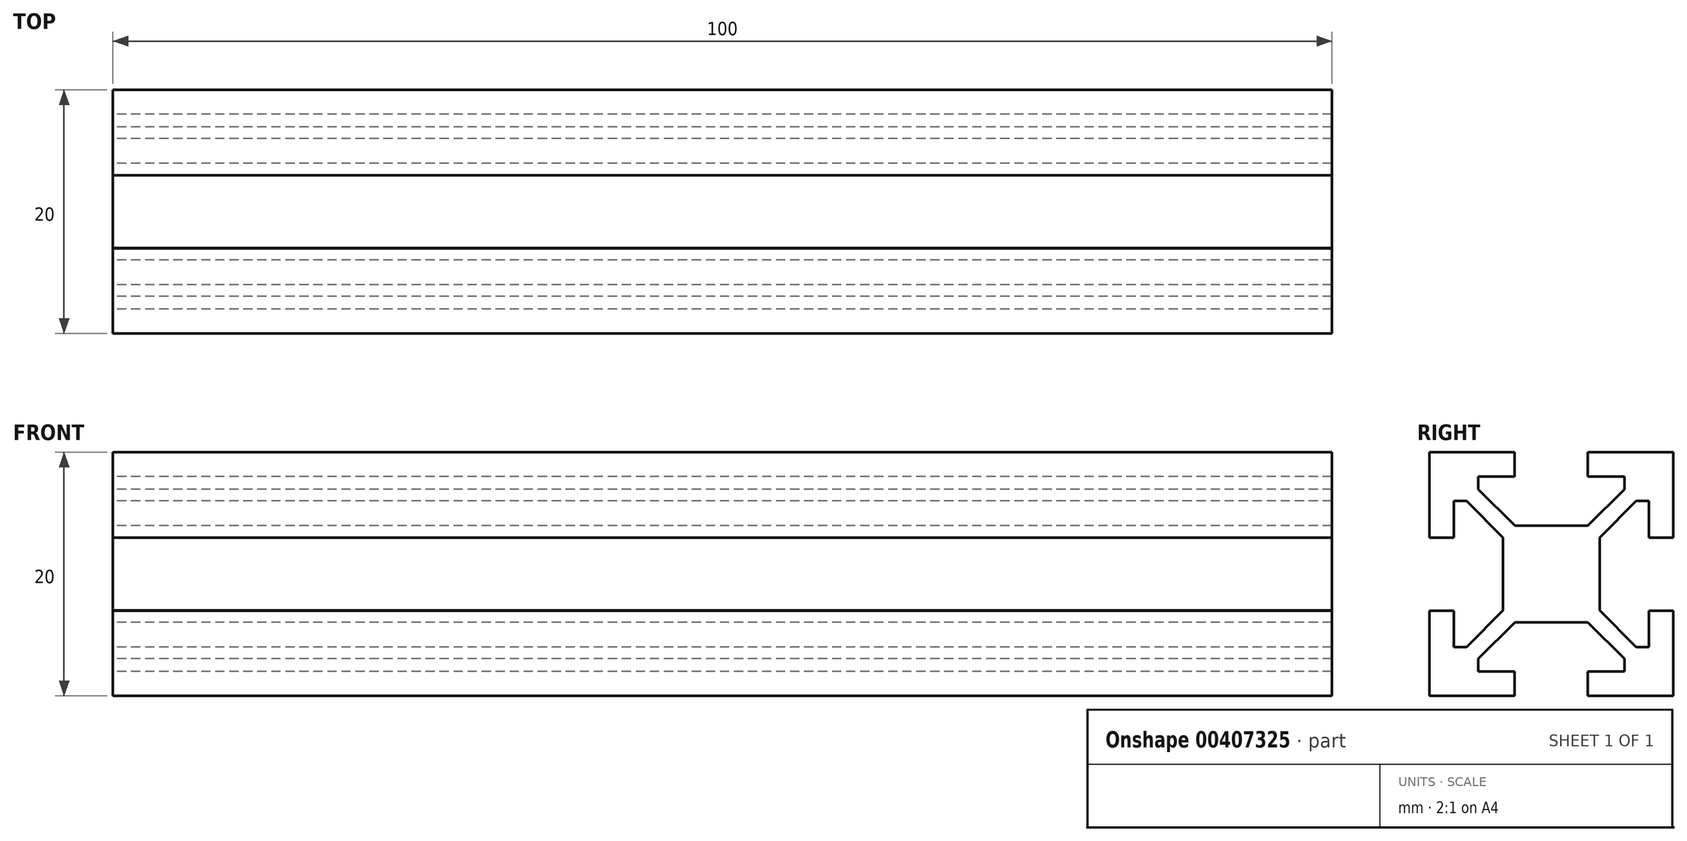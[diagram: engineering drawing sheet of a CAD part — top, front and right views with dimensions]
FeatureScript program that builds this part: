
annotation { "Feature Type Name" : "Feature", "Feature Type Description" : "" }
export const myFeature = defineFeature(function(context is Context, id is Id, definition is map)
    precondition{}
    {
        {
            var Q0;
            Q0=qCreatedBy(makeId("Right.planeOp"),FACE);
            var sketch = newSketch(context, id + "F0", { "sketchPlane" : qUnion([Q0])});
            skLineSegment(sketch, "E0", {"start": v(0, 3.96) * mm, "end": v(-3, 3.96) * mm});
            skLineSegment(sketch, "E1", {"start": v(-3, 3.96) * mm, "end": v(-6, 6.96) * mm});
            skLineSegment(sketch, "E2", {"start": v(-6, 6.96) * mm, "end": v(-6, 8) * mm});
            skLineSegment(sketch, "E3", {"start": v(-6, 8) * mm, "end": v(-3, 8) * mm});
            skLineSegment(sketch, "E4", {"start": v(-3, 8) * mm, "end": v(-3, 10) * mm});
            skLineSegment(sketch, "E5", {"start": v(-3, 10) * mm, "end": v(-10, 10) * mm});
            skLineSegment(sketch, "E6", {"start": v(0, 3.96) * mm, "end": v(0, 0) * mm, "construction": true});
            skLineSegment(sketch, "E7.MirrorCS", {"start": v(3, 8) * mm, "end": v(3, 10) * mm});
            skLineSegment(sketch, "E8.MirrorCS", {"start": v(6, 6.96) * mm, "end": v(6, 8) * mm});
            skLineSegment(sketch, "E9.MirrorCS", {"start": v(6, 8) * mm, "end": v(3, 8) * mm});
            skLineSegment(sketch, "E10.MirrorCS", {"start": v(0, 3.96) * mm, "end": v(3, 3.96) * mm});
            skLineSegment(sketch, "E11.MirrorCS", {"start": v(3, 10) * mm, "end": v(10, 10) * mm});
            skLineSegment(sketch, "E12.MirrorCS", {"start": v(3, 3.96) * mm, "end": v(6, 6.96) * mm});
            skLineSegment(sketch, "E13.1.0", {"start": v(-10, -3) * mm, "end": v(-10, -10) * mm});
            skLineSegment(sketch, "E13.1.1", {"start": v(-8, 3) * mm, "end": v(-10, 3) * mm});
            skLineSegment(sketch, "E13.1.2", {"start": v(-3.96, 0) * mm, "end": v(-3.96, -3) * mm});
            skLineSegment(sketch, "E13.1.3", {"start": v(-10, 3) * mm, "end": v(-10, 10) * mm});
            skLineSegment(sketch, "E13.1.4", {"start": v(-3.96, -3) * mm, "end": v(-6.96, -6) * mm});
            skLineSegment(sketch, "E13.1.5", {"start": v(-8, -6) * mm, "end": v(-8, -3) * mm});
            skLineSegment(sketch, "E13.1.6", {"start": v(-6.96, -6) * mm, "end": v(-8, -6) * mm});
            skLineSegment(sketch, "E13.1.7", {"start": v(-3.96, 3) * mm, "end": v(-6.96, 6) * mm});
            skLineSegment(sketch, "E13.1.8", {"start": v(-3.96, 0) * mm, "end": v(-3.96, 3) * mm});
            skLineSegment(sketch, "E13.1.9", {"start": v(-6.96, 6) * mm, "end": v(-8, 6) * mm});
            skLineSegment(sketch, "E13.1.10", {"start": v(-8, 6) * mm, "end": v(-8, 3) * mm});
            skLineSegment(sketch, "E13.1.11", {"start": v(-8, -3) * mm, "end": v(-10, -3) * mm});
            skLineSegment(sketch, "E13.2.0", {"start": v(3, -10) * mm, "end": v(10, -10) * mm});
            skLineSegment(sketch, "E13.2.1", {"start": v(-3, -8) * mm, "end": v(-3, -10) * mm});
            skLineSegment(sketch, "E13.2.2", {"start": v(0, -3.96) * mm, "end": v(3, -3.96) * mm});
            skLineSegment(sketch, "E13.2.3", {"start": v(-3, -10) * mm, "end": v(-10, -10) * mm});
            skLineSegment(sketch, "E13.2.4", {"start": v(3, -3.96) * mm, "end": v(6, -6.96) * mm});
            skLineSegment(sketch, "E13.2.5", {"start": v(6, -8) * mm, "end": v(3, -8) * mm});
            skLineSegment(sketch, "E13.2.6", {"start": v(6, -6.96) * mm, "end": v(6, -8) * mm});
            skLineSegment(sketch, "E13.2.7", {"start": v(-3, -3.96) * mm, "end": v(-6, -6.96) * mm});
            skLineSegment(sketch, "E13.2.8", {"start": v(0, -3.96) * mm, "end": v(-3, -3.96) * mm});
            skLineSegment(sketch, "E13.2.9", {"start": v(-6, -6.96) * mm, "end": v(-6, -8) * mm});
            skLineSegment(sketch, "E13.2.10", {"start": v(-6, -8) * mm, "end": v(-3, -8) * mm});
            skLineSegment(sketch, "E13.2.11", {"start": v(3, -8) * mm, "end": v(3, -10) * mm});
            skLineSegment(sketch, "E13.3.0", {"start": v(10, 3) * mm, "end": v(10, 10) * mm});
            skLineSegment(sketch, "E13.3.1", {"start": v(8, -3) * mm, "end": v(10, -3) * mm});
            skLineSegment(sketch, "E13.3.2", {"start": v(3.96, 0) * mm, "end": v(3.96, 3) * mm});
            skLineSegment(sketch, "E13.3.3", {"start": v(10, -3) * mm, "end": v(10, -10) * mm});
            skLineSegment(sketch, "E13.3.4", {"start": v(3.96, 3) * mm, "end": v(6.96, 6) * mm});
            skLineSegment(sketch, "E13.3.5", {"start": v(8, 6) * mm, "end": v(8, 3) * mm});
            skLineSegment(sketch, "E13.3.6", {"start": v(6.96, 6) * mm, "end": v(8, 6) * mm});
            skLineSegment(sketch, "E13.3.7", {"start": v(3.96, -3) * mm, "end": v(6.96, -6) * mm});
            skLineSegment(sketch, "E13.3.8", {"start": v(3.96, 0) * mm, "end": v(3.96, -3) * mm});
            skLineSegment(sketch, "E13.3.9", {"start": v(6.96, -6) * mm, "end": v(8, -6) * mm});
            skLineSegment(sketch, "E13.3.10", {"start": v(8, -6) * mm, "end": v(8, -3) * mm});
            skLineSegment(sketch, "E13.3.11", {"start": v(8, 3) * mm, "end": v(10, 3) * mm});
            skPoint(sketch, "E13.center", {"position": v(0, 0) * mm});
            skLineSegment(sketch, "E14", {"start": v(0, 0) * mm, "end": v(-10, 10) * mm, "construction": true});
            skSolve(sketch);
        }
        {
            var Q0;
            Q0=makeQuery(id+"F0.imprint","IMPRINT",FACE,{"disambiguationData":[TD([[makeQuery(id+"F0.imprint","IMPRINT",EDGE,{"derivedFrom":sQuery(id+"F0.wireOp",EDGE,"E0")}),1.0]])]});
            extrude(context, id + "F1", {"entities" : qUnion([Q0]), "depth" : 100 * mm});
        }
    });
